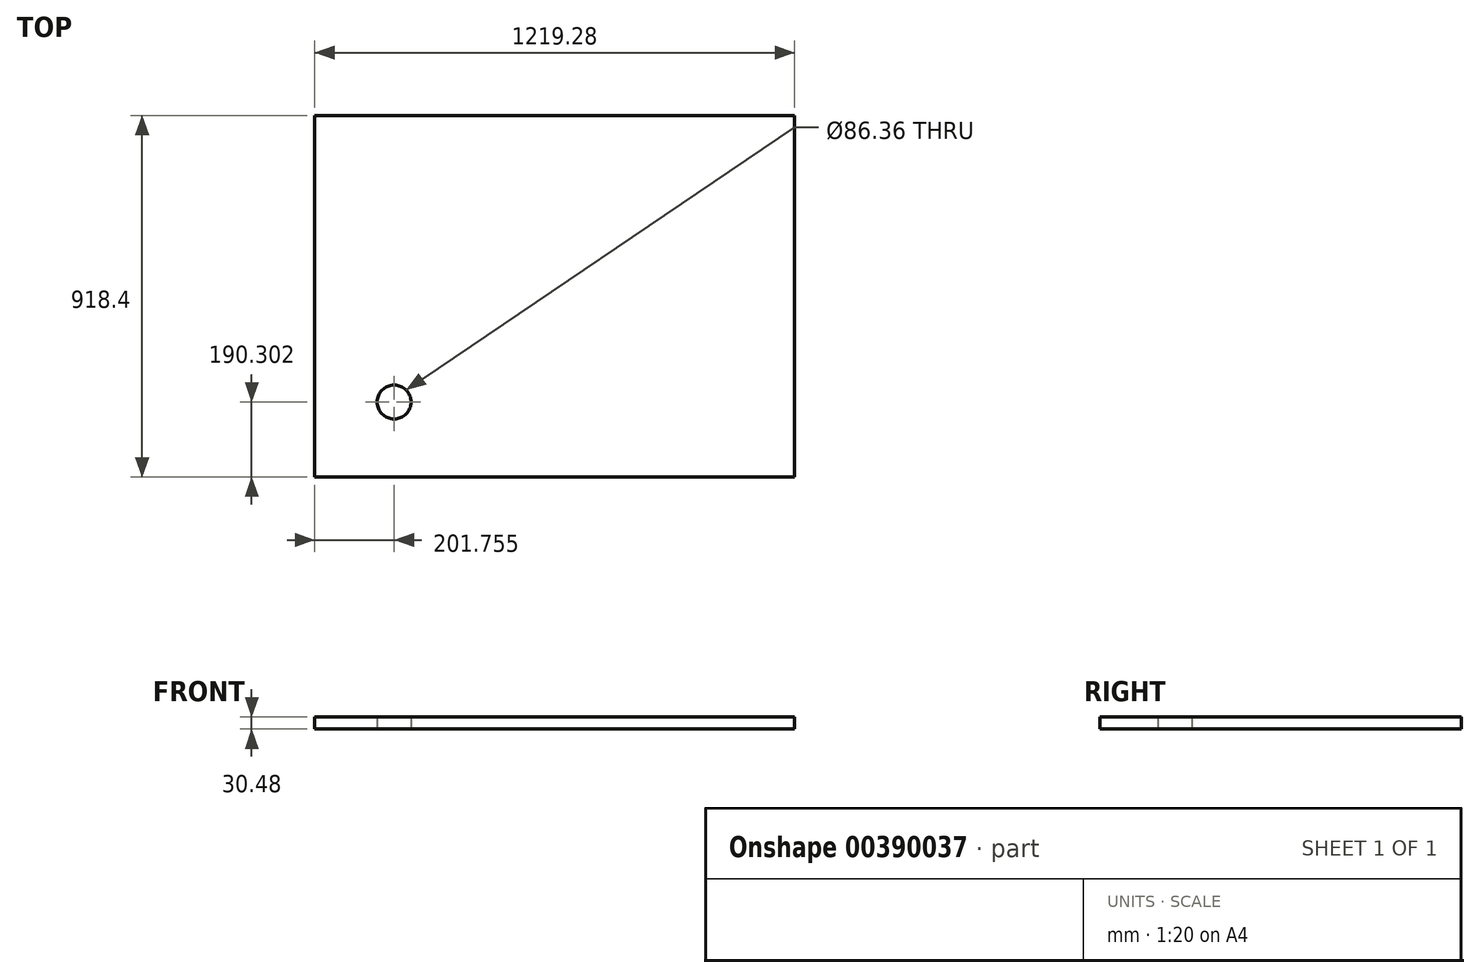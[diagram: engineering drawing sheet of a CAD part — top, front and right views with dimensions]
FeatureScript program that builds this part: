
annotation { "Feature Type Name" : "Feature", "Feature Type Description" : "" }
export const myFeature = defineFeature(function(context is Context, id is Id, definition is map)
    precondition{}
    {
        {
            var Q0;
            Q0=qCreatedBy(makeId("Top.planeOp"),FACE);
            var sketch = newSketch(context, id + "F0", { "sketchPlane" : qUnion([Q0])});
            skLineSegment(sketch, "E0.bottom", {"start": v(-609.64, -459.2) * mm, "end": v(609.64, -459.2) * mm});
            skLineSegment(sketch, "E0.top", {"start": v(-609.64, 459.2) * mm, "end": v(609.64, 459.2) * mm});
            skLineSegment(sketch, "E0.left", {"start": v(-609.64, -459.2) * mm, "end": v(-609.64, 459.2) * mm});
            skLineSegment(sketch, "E0.right", {"start": v(609.64, -459.2) * mm, "end": v(609.64, 459.2) * mm});
            skPoint(sketch, "E0.middle", {"position": v(0, 0) * mm});
            skCircle(sketch, "E1", {"center": v(-407.89, -268.9) * mm, "radius": 43.18 * mm});
            skSolve(sketch);
        }
        {
            var Q0;
            Q0=makeQuery(id+"F0.imprint","IMPRINT",FACE,{"disambiguationData":[TD([[makeQuery(id+"F0.imprint","IMPRINT",EDGE,{"derivedFrom":sQuery(id+"F0.wireOp",EDGE,"E0.bottom")}),1.0]])]});
            extrude(context, id + "F1", {"entities" : qUnion([Q0]), "depth" : 30.48 * mm});
        }
    });
